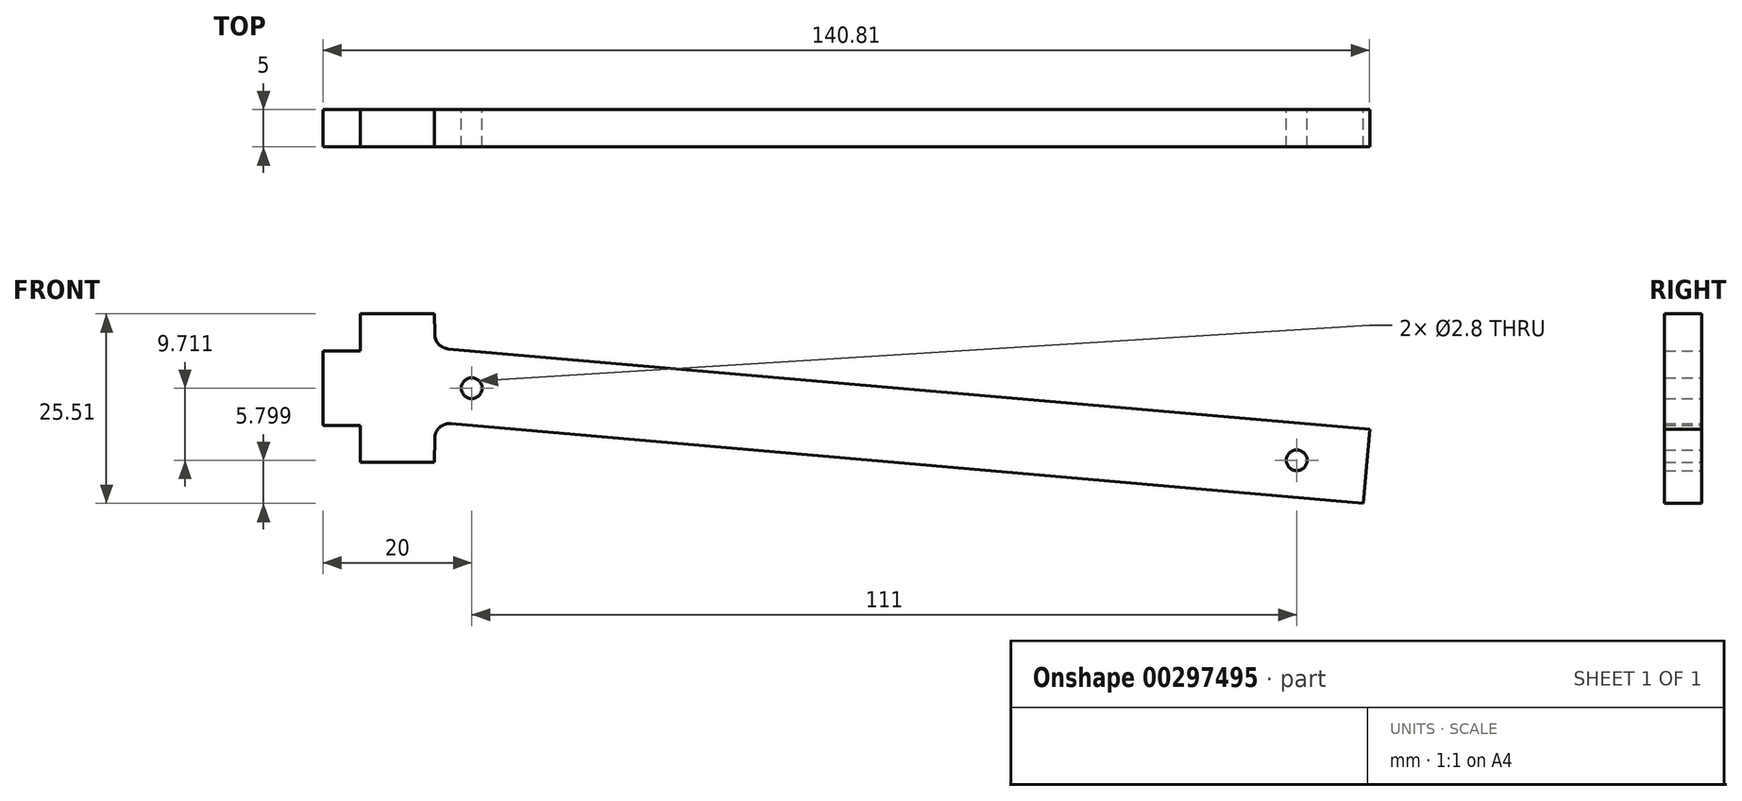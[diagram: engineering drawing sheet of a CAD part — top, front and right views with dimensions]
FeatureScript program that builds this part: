
annotation { "Feature Type Name" : "Feature", "Feature Type Description" : "" }
export const myFeature = defineFeature(function(context is Context, id is Id, definition is map)
    precondition{}
    {
        {
            var Q0;
            Q0=qCreatedBy(makeId("Front.planeOp"),FACE);
            var sketch = newSketch(context, id + "F0", { "sketchPlane" : qUnion([Q0])});
            skCircle(sketch, "E0", {"center": v(0, 0) * mm, "radius": 1.4 * mm});
            skCircle(sketch, "E1", {"center": v(111, -9.71) * mm, "radius": 1.4 * mm});
            skLineSegment(sketch, "E2.bottom", {"start": v(-28.54, -10) * mm, "end": v(-33.54, -10) * mm});
            skLineSegment(sketch, "E2.top", {"start": v(-28.54, 10) * mm, "end": v(-33.54, 10) * mm});
            skLineSegment(sketch, "E2.left", {"start": v(-28.54, -10) * mm, "end": v(-28.54, 10) * mm});
            skLineSegment(sketch, "E2.right", {"start": v(-33.54, -10) * mm, "end": v(-33.54, 10) * mm});
            skPoint(sketch, "E2.middle", {"position": v(-31.04, 0) * mm});
            skLineSegment(sketch, "E3", {"start": v(-28.54, -10) * mm, "end": v(-23.54, -10) * mm});
            skLineSegment(sketch, "E4", {"start": v(-23.54, -10) * mm, "end": v(-23.54, 10) * mm});
            skLineSegment(sketch, "E5", {"start": v(-23.54, 10) * mm, "end": v(-28.54, 10) * mm});
            skLineSegment(sketch, "E6.bottom", {"start": v(-20, 5) * mm, "end": v(-15, 5) * mm});
            skLineSegment(sketch, "E6.top", {"start": v(-20, -5) * mm, "end": v(-15, -5) * mm});
            skLineSegment(sketch, "E6.left", {"start": v(-20, 5) * mm, "end": v(-20, -5) * mm});
            skPoint(sketch, "E6.middle", {"position": v(-17.5, 0) * mm});
            skPoint(sketch, "E6.middle.positionSnap0", {"position": v(-23.54, 0) * mm});
            skPoint(sketch, "E6.centerSnap0", {"position": v(-23.54, 0) * mm});
            skLineSegment(sketch, "E7.bottom", {"start": v(-5, -10) * mm, "end": v(-15, -10) * mm});
            skLineSegment(sketch, "E7.top", {"start": v(-5, 10) * mm, "end": v(-15, 10) * mm});
            skLineSegment(sketch, "E7.right", {"start": v(-15, -10) * mm, "end": v(-15, -5) * mm});
            skLineSegment(sketch, "E8.trimOffspring", {"start": v(-15, 5) * mm, "end": v(-15, 10) * mm});
            skLineSegment(sketch, "E9", {"start": v(0, 0) * mm, "end": v(111, -9.71) * mm});
            skLineSegment(sketch, "E10", {"start": v(-2.8, -4.77) * mm, "end": v(119.94, -15.51) * mm});
            skLineSegment(sketch, "E11", {"start": v(119.94, -15.51) * mm, "end": v(120.81, -5.55) * mm});
            skLineSegment(sketch, "E12", {"start": v(-3.15, 5.3) * mm, "end": v(120.81, -5.55) * mm});
            skLineSegment(sketch, "E13", {"start": v(-5, 10) * mm, "end": v(-4.98, 7.27) * mm});
            skLineSegment(sketch, "E14", {"start": v(-5, -10) * mm, "end": v(-4.98, -6.75) * mm});
            skPoint(sketch, "E15.visualSharp", {"position": v(-4.96, 5.45) * mm});
            skArc(sketch, "E15.filletArc", {"start": v(-4.98, 7.27) * mm, "mid": v(-4.44, 5.93) * mm, "end": v(-3.15, 5.3) * mm});
            skPoint(sketch, "E16.visualSharp", {"position": v(-4.96, -4.58) * mm});
            skArc(sketch, "E16.filletArc", {"start": v(-2.8, -4.77) * mm, "mid": v(-4.32, -5.29) * mm, "end": v(-4.98, -6.75) * mm});
            skSolve(sketch);
        }
        {
            var Q0;
            Q0=makeQuery(id+"F0.imprint","IMPRINT",FACE,{"disambiguationData":[TD([[makeQuery(id+"F0.imprint","IMPRINT",EDGE,{"derivedFrom":sQuery(id+"F0.wireOp",EDGE,"E0")}),-1.0]])]});
            extrude(context, id + "F1", {"entities" : qUnion([Q0]), "depth" : 5 * mm});
        }
    });
